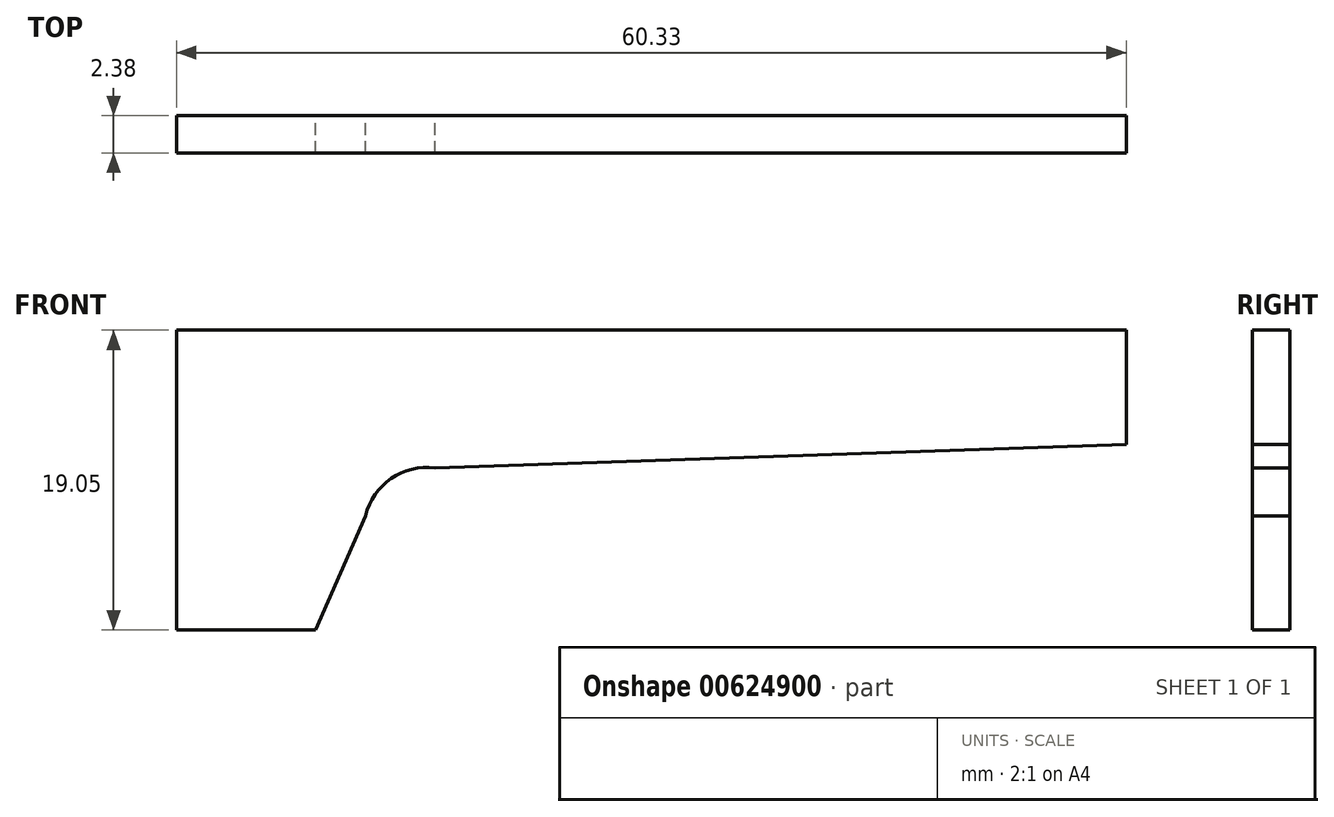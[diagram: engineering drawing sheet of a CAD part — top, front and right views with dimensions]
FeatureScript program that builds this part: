
annotation { "Feature Type Name" : "Feature", "Feature Type Description" : "" }
export const myFeature = defineFeature(function(context is Context, id is Id, definition is map)
    precondition{}
    {
        {
            var Q0;
            Q0=qCreatedBy(makeId("Front.planeOp"),FACE);
            var sketch = newSketch(context, id + "F0", { "sketchPlane" : qUnion([Q0])});
            skLineSegment(sketch, "E0.bottom", {"start": v(0, 0) * mm, "end": v(60.33, 0) * mm});
            skLineSegment(sketch, "E0.top", {"start": v(0, 19.05) * mm, "end": v(60.33, 19.05) * mm});
            skLineSegment(sketch, "E0.left", {"start": v(0, 0) * mm, "end": v(0, 19.05) * mm});
            skLineSegment(sketch, "E0.right", {"start": v(60.33, 0) * mm, "end": v(60.33, 19.05) * mm});
            skSolve(sketch);
        }
        {
            var Q0;
            Q0=qCreatedBy(makeId("Front.planeOp"),FACE);
            var sketch = newSketch(context, id + "F1", { "sketchPlane" : qUnion([Q0])});
            skCircle(sketch, "E1", {"center": v(15.88, 6.35) * mm, "radius": 3.97 * mm});
            skLineSegment(sketch, "E2", {"start": v(12.01, 7.25) * mm, "end": v(8.84, 0) * mm});
            skLineSegment(sketch, "E3", {"start": v(16.42, 10.28) * mm, "end": v(60.46, 11.78) * mm});
            skLineSegment(sketch, "E4", {"start": v(60.46, 11.78) * mm, "end": v(60.46, 0) * mm});
            skLineSegment(sketch, "E5", {"start": v(60.46, 0) * mm, "end": v(8.84, 0) * mm});
            skArc(sketch, "E6", {"start": v(16.42, 10.28) * mm, "mid": v(13.78, 9.41) * mm, "end": v(12.01, 7.25) * mm});
            skSolve(sketch);
        }
        {
            var Q0;
            Q0 = qSketchRegion(id + "F1", true);
            var Q1;
            Q1 = qSketchRegion(id + "F0", true);
            extrude(context, id + "F2", {"entities" : qUnion([Q0, Q1]), "depth" : 2.38 * mm, "offsetDistance" : 25.4 * mm});
        }
        {
            var Q0;
            Q0 = qSketchRegion(id + "F1", true);
            extrude(context, id + "F3", {"entities" : qUnion([Q0]), "operationType" : NewBodyOperationType.REMOVE, "depth" : 25.4 * mm, "offsetDistance" : 25.4 * mm});
        }
    });
